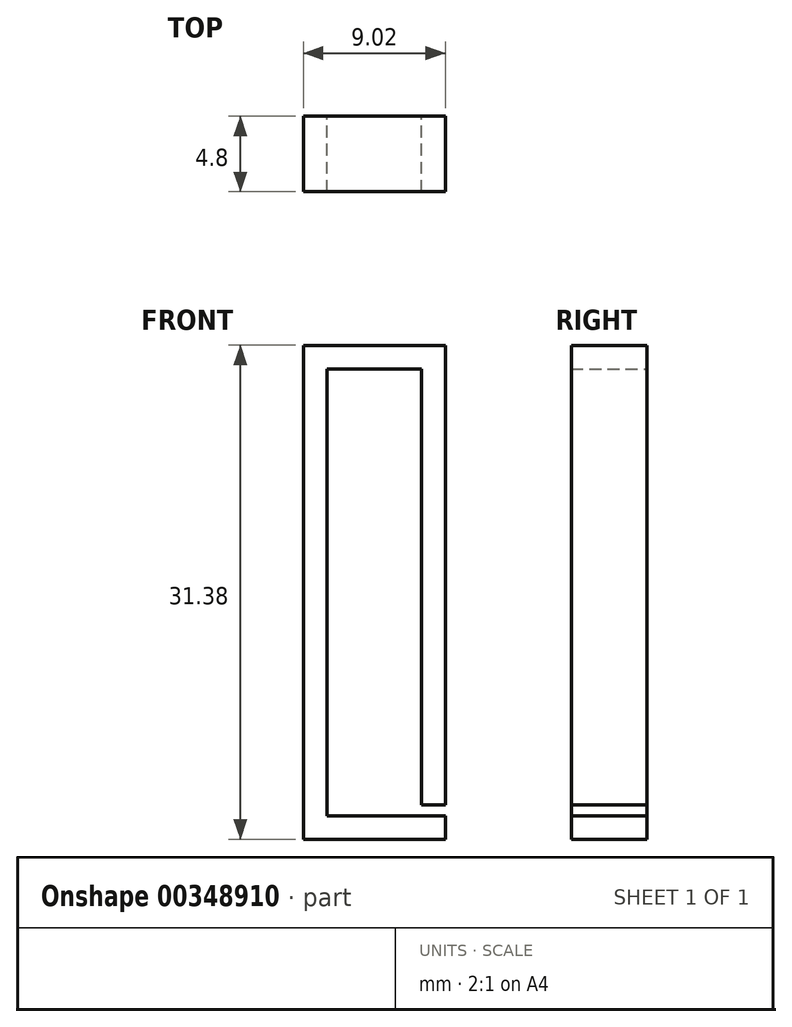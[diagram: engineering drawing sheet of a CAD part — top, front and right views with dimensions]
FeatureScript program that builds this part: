
annotation { "Feature Type Name" : "Feature", "Feature Type Description" : "" }
export const myFeature = defineFeature(function(context is Context, id is Id, definition is map)
    precondition{}
    {
        {
            var Q0;
            Q0=qCreatedBy(makeId("Front.planeOp"),FACE);
            var sketch = newSketch(context, id + "F0", { "sketchPlane" : qUnion([Q0])});
            skLineSegment(sketch, "E0.bottom", {"start": v(-4.41, 14.59) * mm, "end": v(4.6, 14.59) * mm});
            skLineSegment(sketch, "E0.top", {"start": v(-4.41, -16.8) * mm, "end": v(4.6, -16.8) * mm});
            skLineSegment(sketch, "E0.left", {"start": v(-4.41, 14.59) * mm, "end": v(-4.41, -16.8) * mm});
            skLineSegment(sketch, "E0.right", {"start": v(4.6, 14.59) * mm, "end": v(4.6, -16.8) * mm});
            skLineSegment(sketch, "E1.0", {"start": v(-2.9, 13.09) * mm, "end": v(3.1, 13.09) * mm});
            skLineSegment(sketch, "E1.1", {"start": v(-2.9, 13.09) * mm, "end": v(-2.9, -15.29) * mm});
            skLineSegment(sketch, "E1.2", {"start": v(-2.9, -15.29) * mm, "end": v(3.1, -15.29) * mm});
            skLineSegment(sketch, "E1.3", {"start": v(3.1, 13.09) * mm, "end": v(3.1, -15.29) * mm});
            skLineSegment(sketch, "E2", {"start": v(3.1, -14.6) * mm, "end": v(4.6, -14.6) * mm});
            skLineSegment(sketch, "E3", {"start": v(4.6, -14.6) * mm, "end": v(4.6, -15.29) * mm});
            skLineSegment(sketch, "E4", {"start": v(4.6, -15.29) * mm, "end": v(3.1, -15.29) * mm});
            skSolve(sketch);
        }
        {
            var Q0;
            {var subQ7=sQuery(id+"F0.wireOp",EDGE,"E0.bottom");Q0=makeQuery(id+"F0.imprint","IMPRINT",FACE,{"disambiguationData":[TD([[makeQuery(id+"F0.imprint","IMPRINT",EDGE,{"derivedFrom":subQ7}),-1.0]])]});}
            extrude(context, id + "F1", {"entities" : qUnion([Q0]), "depth" : 4.8 * mm});
        }
    });
